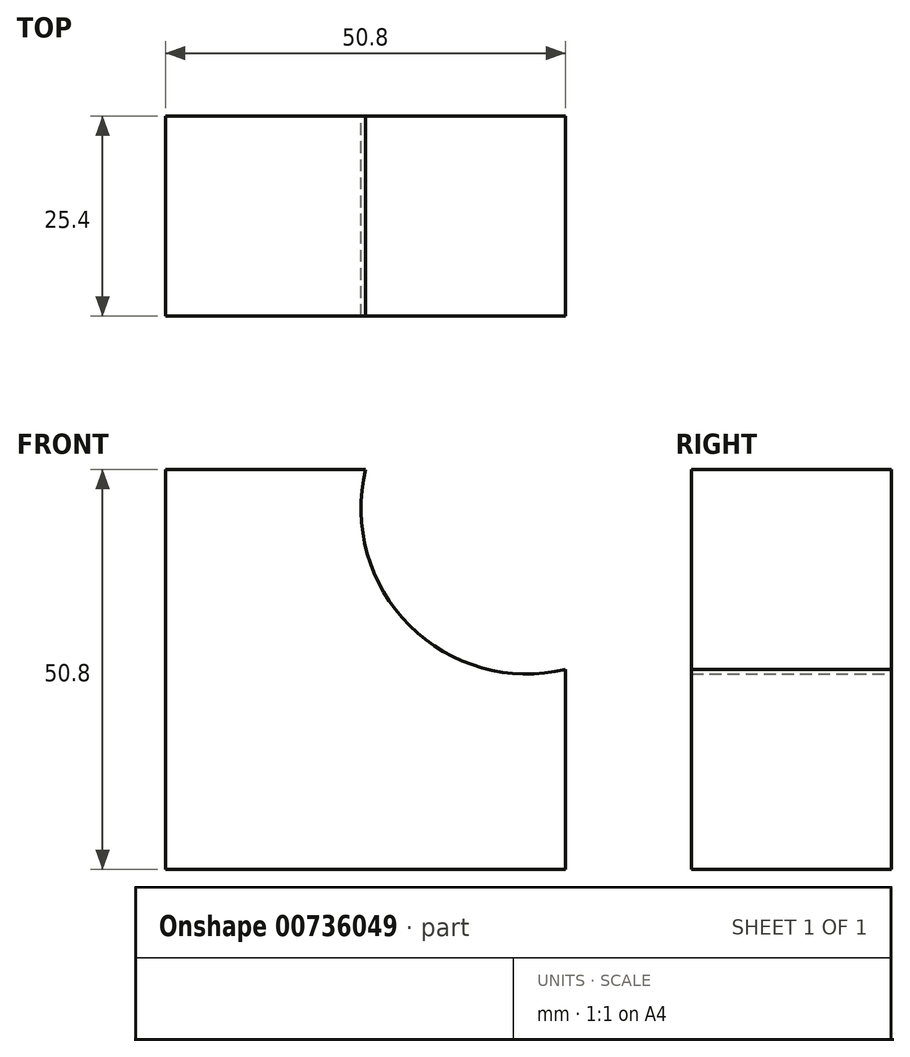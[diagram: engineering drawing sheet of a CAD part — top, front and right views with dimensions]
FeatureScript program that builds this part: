
annotation { "Feature Type Name" : "Feature", "Feature Type Description" : "" }
export const myFeature = defineFeature(function(context is Context, id is Id, definition is map)
    precondition{}
    {
        {
            var Q0;
            Q0=qCreatedBy(makeId("Front.planeOp"),FACE);
            var sketch = newSketch(context, id + "F0", { "sketchPlane" : qUnion([Q0])});
            skLineSegment(sketch, "E0", {"start": v(-47.07, 42.88) * mm, "end": v(-47.07, -7.92) * mm});
            skLineSegment(sketch, "E1", {"start": v(-47.07, -7.92) * mm, "end": v(3.73, -7.92) * mm});
            skLineSegment(sketch, "E2", {"start": v(-47.07, 42.88) * mm, "end": v(-21.67, 42.88) * mm});
            skLineSegment(sketch, "E3", {"start": v(3.73, -7.92) * mm, "end": v(3.73, 17.48) * mm});
            skArc(sketch, "E4", {"start": v(-21.67, 42.88) * mm, "mid": v(-16.08, 23.07) * mm, "end": v(3.73, 17.48) * mm});
            skSolve(sketch);
        }
        {
            var Q0;
            Q0=qSketchRegion(id+"F0",true);
            extrude(context, id + "F1", {"entities" : qUnion([Q0]), "depth" : 25.4 * mm, "offsetDistance" : 25.4 * mm});
        }
    });
